# Revit family: JC KONTAKTER JCK117AT DE
name_source: partatom
category: Specialty Equipment
units: mm (PartAtom-declared; Revit-internal decimal feet)

## family parameters
Cut with Voids When Loaded = No
Enable Cutting in Views = Yes
Host = Face
Maintain Annotation Orientation = Yes
Part Type = Normal
Room Calculation Point = No
Round Connector Dimension = Use Diameter
Shared = No

## types (1)
- JCK117AT
    Anzahl der mikroschalter = 2
    Deckel = Edelstahl
    Default Elevation = 800 mm  [stored 2.62467 ft]
    Description = Schlichter, robuster Großflächentaster mit flacher Druckplatte aus rostfreiem Metall und Unterteil aus silbereloxiertem Aluminium.
Das Modell wurde speziell für den Einsatz in exklusiven Umgebungen sowie in denkmalgeschützten Gebäuden entwickelt.

Kann optional drahtlos ausgeführt werden, was besonders in älteren Gebäuden von Vorteil ist, da das Verlegen von Kabeln dort oft schwierig ist.
    Endkappen = Plastik
    Geringster nennstrom = 1mA/4 V DC
    Herstellungsland = Schweden
    Kern = Aluminum ENAW 6060
    Manufacturer = JC Kontakter
    Mikroschalter = Standard NO IP67
    Model = JCK117AT
    Nomineller nennstrom = 12 V - Resistive 6A Inductive L/R 5ms 6A, 24 V - Resistive 6A Inductive L/R 5ms 5A
    Power factor = 1
    Produktgewicht = 0.410 kg
    Technisches Produktblatt = https://grossflaechentaster.de
    URL = https://grossflaechentaster.de
    Voltage = 24 V

note: [stored X ft] marks values corroborated as IEEE doubles in the binary element streams (Revit-internal decimal feet)

## geometry (parser evidence)
native form markers: Sweep x6
no freeform markers — native parametric forms only
